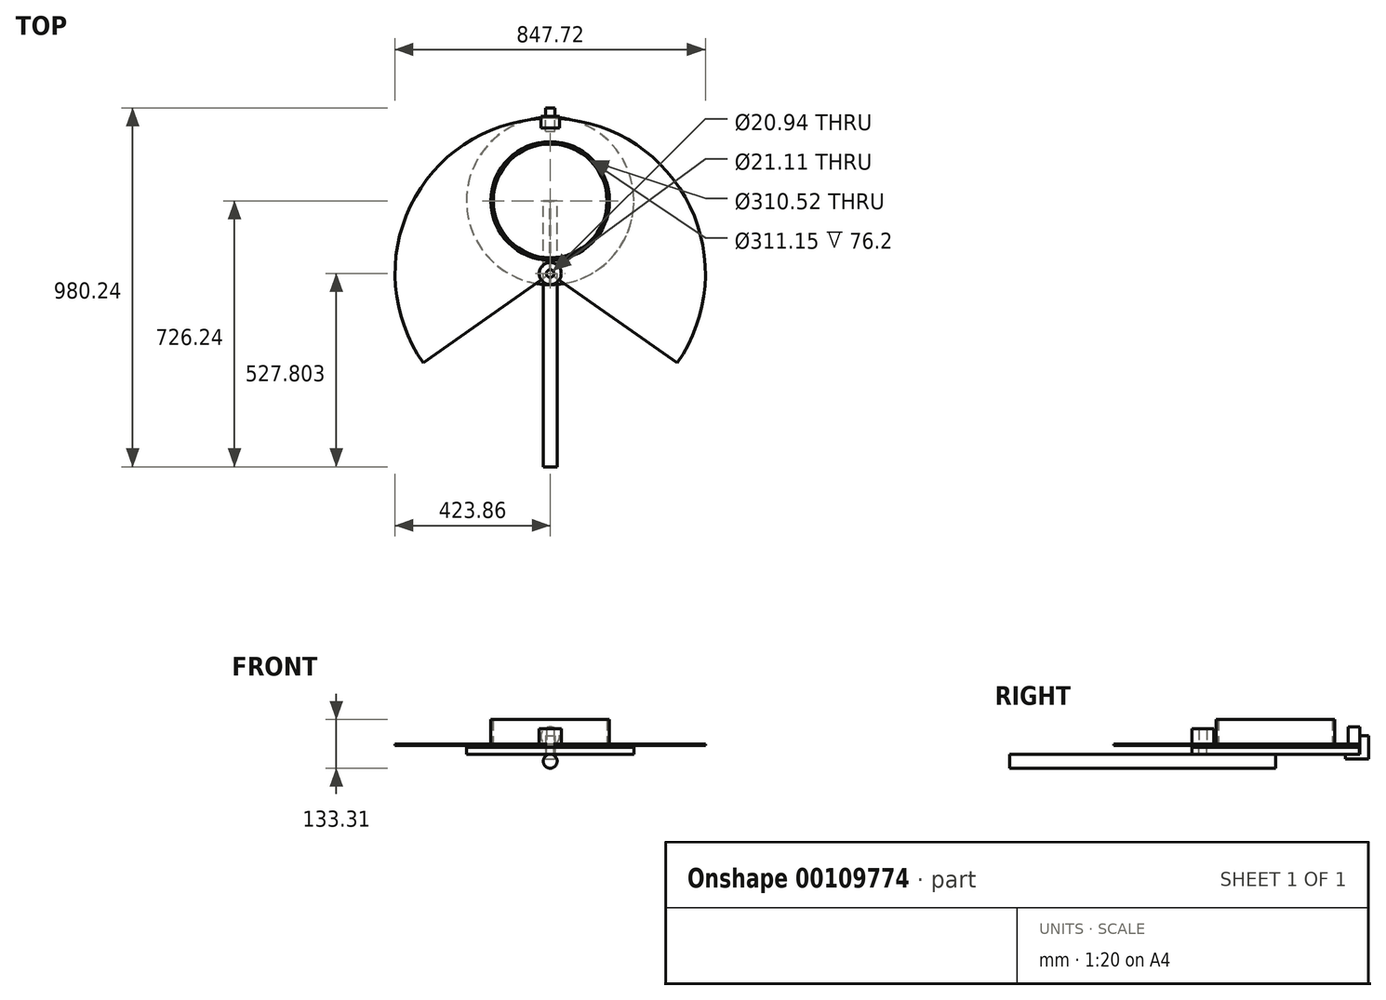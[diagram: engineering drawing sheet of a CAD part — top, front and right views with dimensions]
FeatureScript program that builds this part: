
annotation { "Feature Type Name" : "Feature", "Feature Type Description" : "" }
export const myFeature = defineFeature(function(context is Context, id is Id, definition is map)
    precondition{}
    {
        {
            var Q0;
            Q0=qCreatedBy(makeId("Top.planeOp"),FACE);
            var sketch = newSketch(context, id + "F0", { "sketchPlane" : qUnion([Q0])});
            skCircle(sketch, "E0", {"center": v(0, 0) * mm, "radius": 161.93 * mm});
            skCircle(sketch, "E1.0", {"center": v(0, 0) * mm, "radius": 155.57 * mm});
            skSolve(sketch);
        }
        {
            var Q0;
            Q0=makeQuery(id+"F0.imprint","IMPRINT",FACE,{"disambiguationData":[TD([[makeQuery(id+"F0.imprint","IMPRINT",EDGE,{"derivedFrom":sQuery(id+"F0.wireOp",EDGE,"E0")}),1.0]])]});
            extrude(context, id + "F1", {"entities" : qUnion([Q0]), "depth" : 76.2 * mm});
        }
        {
            var Q0;
            Q0=qCreatedBy(makeId("Top.planeOp"),FACE);
            var sketch = newSketch(context, id + "F2", { "sketchPlane" : qUnion([Q0])});
            skCircle(sketch, "E2", {"center": v(0, 0) * mm, "radius": 228.6 * mm});
            skSolve(sketch);
        }
        {
            var Q0;
            Q0=makeQuery(id+"F2.imprint","IMPRINT",FACE,{"disambiguationData":[TD([[makeQuery(id+"F2.imprint","IMPRINT",EDGE,{"derivedFrom":sQuery(id+"F2.wireOp",EDGE,"E2")}),1.0]])]});
            extrude(context, id + "F3", {"entities" : qUnion([Q0]), "oppositeDirection" : true, "depth" : 19.05 * mm});
        }
        {
            var Q0;
            Q0=makeQuery(id+"F3.opExtrude","CAP_FACE",FACE,{"disambiguationData":[OSD([sQuery(id+"F2.wireOp",EDGE,"E2")])],"isStart":true});
            var sketch = newSketch(context, id + "F4", { "sketchPlane" : qUnion([Q0])});
            skLineSegment(sketch, "E3", {"start": v(0, -228.6) * mm, "end": v(0, -161.93) * mm, "construction": true});
            skCircle(sketch, "E4", {"center": v(0, 0) * mm, "radius": 161.93 * mm, "construction": true});
            skCircle(sketch, "E5", {"center": v(0, -198.44) * mm, "radius": 30.16 * mm});
            skCircle(sketch, "E6", {"center": v(0, -198.44) * mm, "radius": 10.47 * mm});
            skSolve(sketch);
        }
        {
            var Q0;
            Q0 = qSketchRegion(id + "F4", true);
            extrude(context, id + "F5", {"entities" : qUnion([Q0]), "depth" : 50.8 * mm});
        }
        {
            var Q0;
            Q0=makeQuery(id+"F3.opExtrude","CAP_FACE",FACE,{"disambiguationData":[OSD([sQuery(id+"F2.wireOp",EDGE,"E2")])],"isStart":true});
            cPlane(context, id + "F6", {"entities" : qUnion([Q0]), "cplaneType" : CPlaneType.OFFSET, "offset" : 4.76 * mm, "width" : 152.4 * mm, "height" : 152.4 * mm});
        }
        {
            var Q0;
            Q0=makeQuery(id+"F3.opExtrude","CAP_FACE",FACE,{"disambiguationData":[OSD([sQuery(id+"F2.wireOp",EDGE,"E2")])],"isStart":false});
            var sketch = newSketch(context, id + "F7", { "sketchPlane" : qUnion([Q0])});
            skLineSegment(sketch, "E7", {"start": v(0, -266.7) * mm, "end": v(0, 0) * mm, "construction": true});
            skLineSegment(sketch, "E8.bottom", {"start": v(-12.7, -190.5) * mm, "end": v(12.7, -190.5) * mm});
            skLineSegment(sketch, "E8.top", {"start": v(-12.7, -254) * mm, "end": v(12.7, -254) * mm});
            skLineSegment(sketch, "E8.left", {"start": v(-12.7, -190.5) * mm, "end": v(-12.7, -254) * mm});
            skLineSegment(sketch, "E8.right", {"start": v(12.7, -190.5) * mm, "end": v(12.7, -254) * mm});
            skSolve(sketch);
        }
        {
            var Q0;
            {var subQ0=sQuery(id+"F7.wireOp",EDGE,"E8.top");Q0=makeQuery(id+"F7.imprint","IMPRINT",FACE,{"disambiguationData":[TD([[makeQuery(id+"F7.imprint","IMPRINT",EDGE,{"derivedFrom":subQ0}),1.0]])]});}
            var sketch = newSketch(context, id + "F8", { "sketchPlane" : qUnion([Q0])});
            skLineSegment(sketch, "E9.bottom", {"start": v(12.77, -254.01) * mm, "end": v(-12.7, -254.01) * mm});
            skLineSegment(sketch, "E9.top", {"start": v(12.77, -230.42) * mm, "end": v(-12.7, -230.42) * mm});
            skLineSegment(sketch, "E9.left", {"start": v(12.77, -254.01) * mm, "end": v(12.77, -230.42) * mm});
            skLineSegment(sketch, "E9.right", {"start": v(-12.7, -254.01) * mm, "end": v(-12.7, -230.42) * mm});
            skSolve(sketch);
        }
        {
            var Q0;
            Q0 = qSketchRegion(id + "F7", true);
            extrude(context, id + "F9", {"entities" : qUnion([Q0]), "operationType" : NewBodyOperationType.ADD, "depth" : 12.7 * mm});
        }
        {
            var Q0;
            {var subQ0=sQuery(id+"F8.wireOp",EDGE,"E9.right");var subQ1=sQuery(id+"F8.wireOp",EDGE,"E9.top");var subQ2=makeQuery(id+"F8.imprint","INTERSECT",VERTEX,{"derivedFrom":[subQ1,subQ0]});Q0=makeQuery(id+"F8.imprint","IMPRINT",FACE,{"disambiguationData":[TD([[makeQuery(id+"F8.imprint","IMPRINT",EDGE,{"disambiguationData":[TD([[subQ2,1.0]])],"derivedFrom":subQ0}),-1.0]])]});}
            extrude(context, id + "F10", {"entities" : qUnion([Q0]), "operationType" : NewBodyOperationType.ADD, "oppositeDirection" : true, "depth" : 50.8 * mm});
        }
        {
            var Q0;
            Q0=makeQuery(id+"F10.opExtrude","SWEPT_FACE",FACE,{"disambiguationData":[OSD([sQuery(id+"F8.wireOp",EDGE,"E9.top")])]});
            var sketch = newSketch(context, id + "F11", { "sketchPlane" : qUnion([Q0])});
            skPoint(sketch, "E10.centerSnap0", {"position": v(-20.53, 34.06) * mm});
            skCircle(sketch, "E11", {"center": v(0, 30.16) * mm, "radius": 25.4 * mm});
            skSolve(sketch);
        }
        {
            var Q0;
            Q0 = qSketchRegion(id + "F11", true);
            extrude(context, id + "F12", {"entities" : qUnion([Q0]), "operationType" : NewBodyOperationType.ADD, "depth" : 31.75 * mm});
        }
        {
            var Q0;
            Q0=qCreatedBy(id+"F6.planeOp",FACE);
            var sketch = newSketch(context, id + "F13", { "sketchPlane" : qUnion([Q0])});
            skArc(sketch, "E12", {"start": v(347.2, -441.56) * mm, "mid": v(0, 225.42) * mm, "end": v(-347.2, -441.56) * mm});
            skLineSegment(sketch, "E13", {"start": v(-8.49, -204.38) * mm, "end": v(-347.2, -441.56) * mm});
            skLineSegment(sketch, "E14", {"start": v(8.49, -204.38) * mm, "end": v(347.2, -441.56) * mm});
            skLineSegment(sketch, "E15", {"start": v(0, -198.44) * mm, "end": v(0, -651.19) * mm, "construction": true});
            skCircle(sketch, "E16", {"center": v(0, -198.44) * mm, "radius": 10.36 * mm});
            skCircle(sketch, "E17", {"center": v(0, 0) * mm, "radius": 155.26 * mm});
            skSolve(sketch);
        }
        {
            var Q0;
            Q0=makeQuery(id+"F3.opExtrude","CAP_FACE",FACE,{"disambiguationData":[OSD([sQuery(id+"F2.wireOp",EDGE,"E2")])],"isStart":true});
            var sketch = newSketch(context, id + "F14", { "sketchPlane" : qUnion([Q0])});
            skCircle(sketch, "E18", {"center": v(0, -198.44) * mm, "radius": 10.56 * mm});
            skSolve(sketch);
        }
        {
            var Q0;
            Q0 = qSketchRegion(id + "F14", true);
            extrude(context, id + "F15", {"entities" : qUnion([Q0]), "operationType" : NewBodyOperationType.REMOVE, "oppositeDirection" : true, "depth" : 25.4 * mm});
        }
        {
            var Q0;
            Q0=qCreatedBy(makeId("Front.planeOp"),FACE);
            var sketch = newSketch(context, id + "F16", { "sketchPlane" : qUnion([Q0])});
            skCircle(sketch, "E19", {"center": v(0, -38.06) * mm, "radius": 19.05 * mm});
            skSolve(sketch);
        }
        {
            var Q0;
            Q0=makeQuery(id+"F16.imprint","IMPRINT",FACE,{"disambiguationData":[TD([[makeQuery(id+"F16.imprint","IMPRINT",EDGE,{"derivedFrom":sQuery(id+"F16.wireOp",EDGE,"E19")}),1.0]])]});
            extrude(context, id + "F17", {"entities" : qUnion([Q0]), "operationType" : NewBodyOperationType.ADD, "depth" : 726.24 * mm});
        }
        {
            var Q0;
            Q0=makeQuery(id+"F13.imprint","IMPRINT",FACE,{"disambiguationData":[TD([[makeQuery(id+"F13.imprint","IMPRINT",EDGE,{"derivedFrom":sQuery(id+"F13.wireOp",EDGE,"E12")}),1.0]])]});
            extrude(context, id + "F18", {"entities" : qUnion([Q0]), "depth" : 4.76 * mm});
        }
    });
